# Revit family: NBS_WallgateLtd_WtrSplyFitngsForWshBsnsAndTrghs_PBA050-51-2BA
name_source: partatom
category: Plumbing Fixtures
revit_build: Autodesk Revit 2014 (Build: 20130709_2115(x64)
units: mm (PartAtom-declared; Revit-internal decimal feet)

## types (2) — shared parameters
AssetType = Fixed
BodyMaterial = Stainless steel
CableLength = 4000 mm
Description = Electronic activation dual piezo touch button for basins
DurationUnit = year
FaucetFunction = Unset
FaucetOperation = Unset
FaucetType = Unset
Finish = Stainless steel
IfcExportAs = IfcValveType
IfcExportType = FAUCET
IntegralAccessoryOptions = WDC Electronic Controllers, WVPV Vanity Water Valve Pack, WVPB Basin Water Valve Pack, SHB Wall Hung Basin With Exposed Services, MV0001 Thermostatic Mixer Valve, VT1000/2000/3000 Vanity Tops, VBU Undermount Vanity Bowl, WHB-100 Wall Mounted Basin With Concealed Services, VCWHB Vitreous China Wall Hung Basin, ALT-100 Wall Mounted Nozzle, BWN Deck Mounted Basin Water Nozzle
ManufacturerName = Wallgate Ltd
ManufacturerURL = www.wallgate.com
NBSCertification = www.nationalbimlibrary.com/cert/vmq3vper
NBSDescription = Water supply fittings for wash basins and troughs
NBSReference = 45-35-70/371
NominalHeight = 31 mm  [stored 0.101706 ft]
NominalWidth = 31 mm  [stored 0.101706 ft]
Operation = Piezo push button
ProductInformation = www.wallgate.com/document-centre/docmenu-washroom-controls/docmenu-controls-piezo-activation/doccat-piezo-activation-buttons
Size = 21
TestPressure = 0
ThirdPartyCertification = Ministry of Justice Safer Cell Approval
Uniclass2 = 45-31-93/491
ValveMechanism = Unset
ValveOperation = Other
Version = 3
WarrantyDurationParts = 1
WarrantyDurationUnit = year
WaterSupplyFittingMaterial = NBS_Concept
Weight = 0.40 kg
zero-valued in all types: CloseOffRating, FlowCoefficient

## per-type parameters (varying)
| type | BIMObjectName | Features | Name | NominalLength | WallThicknessOptions |
| PBA050-2BA | NBS_WallgateLtd_WaterSupplyFittingsForBasinsAndTroughs_PBA050-2BA | Anti-ligature design, highly vandal-resistant | WaterSupplyFittingsForBasinsAndTroughs_PBA050-2BA_WallgateLtd | 98 mm  [stored 0.321522 ft] | 10-85 mm |
| PBA051-2BA | NBS_WallgateLtd_WaterSupplyFittingsForBasinsAndTroughs_PBA051-2BA | Anti-ligaturedesign, highly vandal-resistant | WaterSupplyFittingsForBasinsAndTroughs_PBA051-2BA_WallgateLtd | 203 mm | 85-190 mm |

note: column(s) folded — value = type name in every type: ModelNumber

note: [stored X ft] marks values corroborated as IEEE doubles in the binary element streams (Revit-internal decimal feet)

## geometry (parser evidence)
native form markers: Sweep x3
no freeform markers — native parametric forms only
